# Revit family: 57_CRD_ME_Ventura_V1C-C
name_source: partatom
category: Mechanical Equipment
units: mm (PartAtom-declared; Revit-internal decimal feet)

## family parameters
Always vertical = Yes
Classification = None
Cut with Voids When Loaded = No
Part Type = Normal
Room Calculation Point = Yes
Round Connector Dimension = Use Diameter
Shared = No
Work Plane-Based = Yes

## types (1)
- Ventura_V1C-C
    Default Elevation = 1219 mm
    Power = 0 VA
    breedte_unit = 520 mm  [stored 1.70604 ft]
    diameter_condensafvoer = 16 mm  [stored 0.0524934 ft]
    diameter_cv = 15 mm  [stored 0.0492126 ft]
    hart_doorvoer_tov_wand = 150 mm
    hart_onderste_doorvoer = 250 mm  [stored 0.82021 ft]
    onderkant_unit_tov_vloerpeil = 0 mm  [stored 0 ft]
    voltage = 0 V

note: [stored X ft] marks values corroborated as IEEE doubles in the binary element streams (Revit-internal decimal feet)

## geometry (parser evidence)
native form markers: Sweep x24
no freeform markers — native parametric forms only
